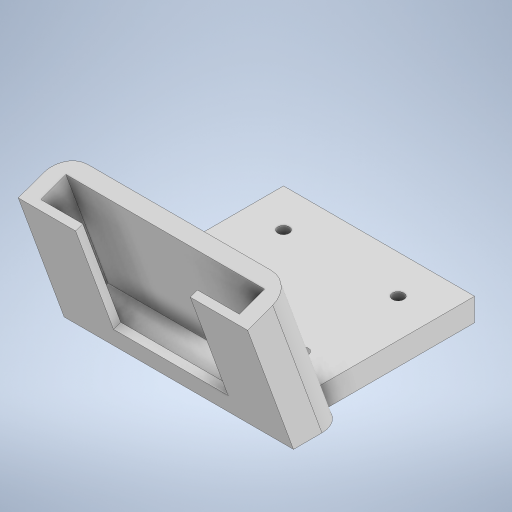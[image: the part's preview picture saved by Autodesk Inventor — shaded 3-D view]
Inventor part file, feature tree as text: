
AUTODESK INVENTOR PART (.ipt)
format: ipt  version: 2024 (Build 280153000, 153)  size: 346,112 bytes
history: native  units: in
note: dims shown in document units (in); Inventor stores cm internally (conversion verified against a paired STEP export)
features: sketch x8, extrude x6, plane x1, sweep x1, fillet x1
ambient origin geometry x8: Origin, YZ Plane, XZ Plane, XY Plane, X Axis, Y Axis, Z Axis, Center Point
bodies: Solid1 (feature_tree)
feature tree (17):
  extrude  "Extrusion1"  Depth=0.5906in
  plane  "Work Plane1"
  extrude  "Extrusion2"  Depth=0.1969in
  extrude  "Extrusion3"  Depth=0.0591in
  extrude  "Extrusion4"  Depth=0.0591in
  extrude  "Extrusion5"  Depth=0.1181in
  sweep  "Sweep1"
  extrude  "Extrusion6"  Depth=0.0787in TaperAngle=0.0deg
  fillet  "Fillet1"  Radius=0.6299in
  sketch  "Sketch1"  dims[d0=0.4921in d1=0.5906in]
  sketch  "Sketch2"  dims[d2=0.1969in d3=0.1969in]
  sketch  "Sketch3"  dims[d4=0.0591in d5=0.0591in]
  sketch  "Sketch4"  dims[d6=0.0591in d7=0.0591in]
  sketch  "Sketch5"  dims[d8=0.1181in d9=0.0in d10=0.7559in]
  sketch  "Sketch6"  dims[d11=0.748in d12=0.6299in]
  sketch  "3D Sketch1"
  sketch  "Sketch7"  dims[d13=1.1811in d14=0.0787in d15=0.0in d16=0.6299in d17=1.0236in d18=0.0787in d19=0.1378in d20=0.0in d21=0.5906in d23=0.1378in d24=0.0394in d25=0.0in d26=0.0394in d27=0.0in d28=0.0in d29=0.0in d30=0.0in d31=0.0in d32=0.1181in]
